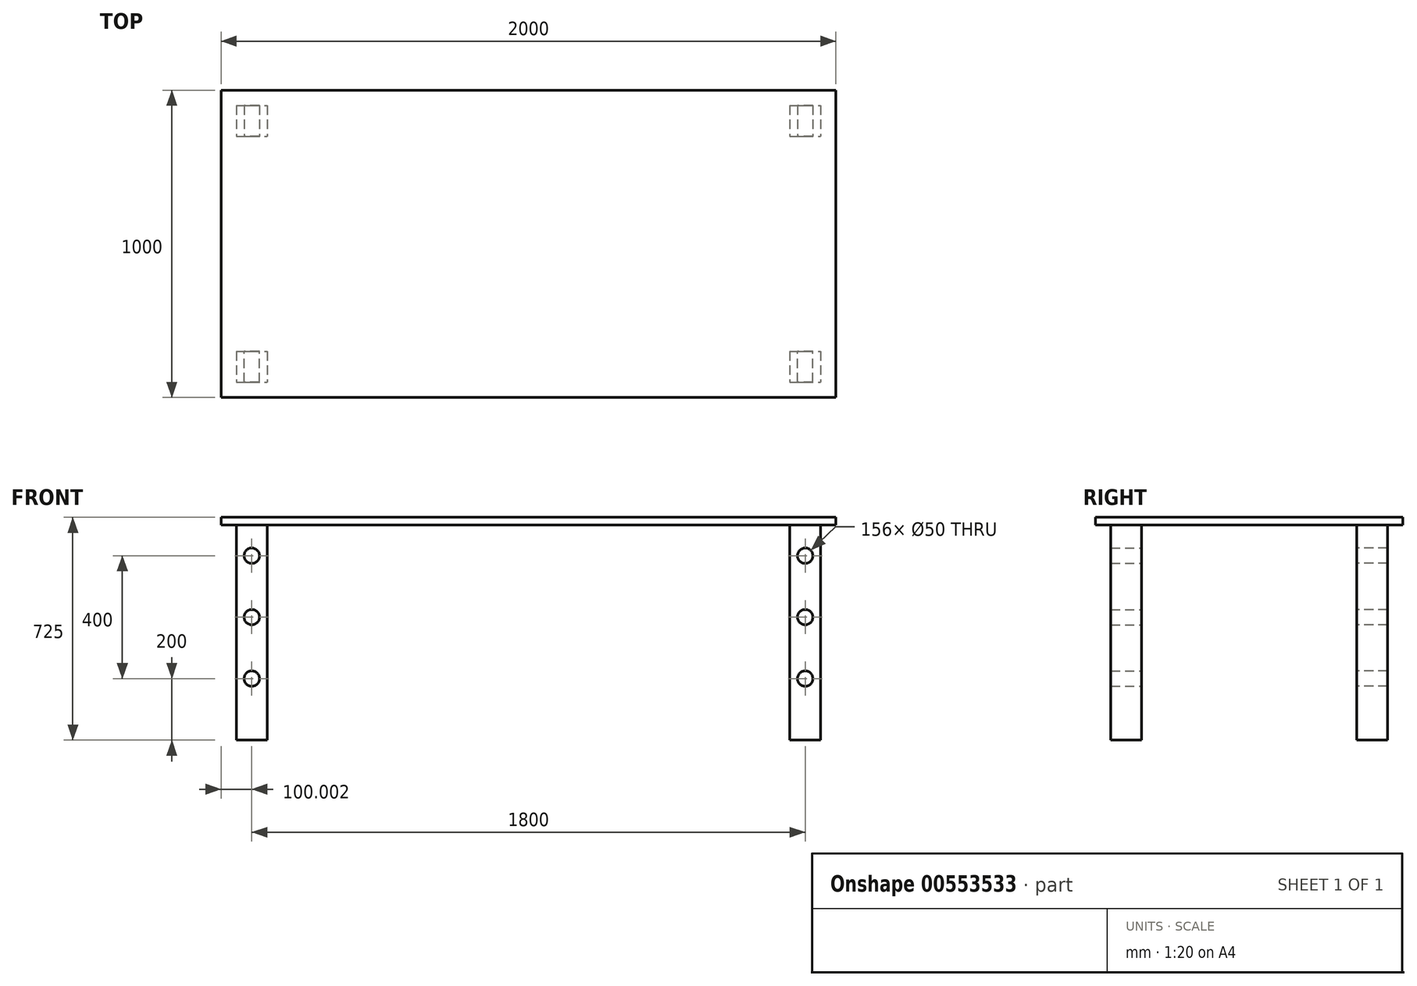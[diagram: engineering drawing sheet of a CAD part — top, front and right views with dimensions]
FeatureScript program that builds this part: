
annotation { "Feature Type Name" : "Feature", "Feature Type Description" : "" }
export const myFeature = defineFeature(function(context is Context, id is Id, definition is map)
    precondition{}
    {
        {
            var Q0;
            Q0=qCreatedBy(makeId("Top.planeOp"),FACE);
            var sketch = newSketch(context, id + "F0", { "sketchPlane" : qUnion([Q0])});
            skLineSegment(sketch, "E0.bottom", {"start": v(-1007.05, 533.18) * mm, "end": v(992.95, 533.18) * mm});
            skLineSegment(sketch, "E0.top", {"start": v(-1007.05, -466.82) * mm, "end": v(992.95, -466.82) * mm});
            skLineSegment(sketch, "E0.left", {"start": v(-1007.05, 533.18) * mm, "end": v(-1007.05, -466.82) * mm});
            skLineSegment(sketch, "E0.right", {"start": v(992.95, 533.18) * mm, "end": v(992.95, -466.82) * mm});
            skLineSegment(sketch, "E1.bottom", {"start": v(-957.05, 483.18) * mm, "end": v(-857.05, 483.18) * mm});
            skLineSegment(sketch, "E1.top", {"start": v(-957.05, 383.18) * mm, "end": v(-857.05, 383.18) * mm});
            skLineSegment(sketch, "E1.left", {"start": v(-957.05, 483.18) * mm, "end": v(-957.05, 383.18) * mm});
            skLineSegment(sketch, "E1.right", {"start": v(-857.05, 483.18) * mm, "end": v(-857.05, 383.18) * mm});
            skLineSegment(sketch, "E2.bottom", {"start": v(-957.05, -316.82) * mm, "end": v(-857.05, -316.82) * mm});
            skLineSegment(sketch, "E2.top", {"start": v(-957.05, -416.82) * mm, "end": v(-857.05, -416.82) * mm});
            skLineSegment(sketch, "E2.left", {"start": v(-957.05, -316.82) * mm, "end": v(-957.05, -416.82) * mm});
            skLineSegment(sketch, "E2.right", {"start": v(-857.05, -316.82) * mm, "end": v(-857.05, -416.82) * mm});
            skLineSegment(sketch, "E3.bottom", {"start": v(842.95, 483.18) * mm, "end": v(942.95, 483.18) * mm});
            skLineSegment(sketch, "E3.top", {"start": v(842.95, 383.18) * mm, "end": v(942.95, 383.18) * mm});
            skLineSegment(sketch, "E3.left", {"start": v(842.95, 483.18) * mm, "end": v(842.95, 383.18) * mm});
            skLineSegment(sketch, "E3.right", {"start": v(942.95, 483.18) * mm, "end": v(942.95, 383.18) * mm});
            skLineSegment(sketch, "E4.bottom", {"start": v(842.95, -316.82) * mm, "end": v(942.95, -316.82) * mm});
            skLineSegment(sketch, "E4.top", {"start": v(842.95, -416.82) * mm, "end": v(942.95, -416.82) * mm});
            skLineSegment(sketch, "E4.left", {"start": v(842.95, -316.82) * mm, "end": v(842.95, -416.82) * mm});
            skLineSegment(sketch, "E4.right", {"start": v(942.95, -316.82) * mm, "end": v(942.95, -416.82) * mm});
            skSolve(sketch);
        }
        {
            var Q0;
            Q0=makeQuery(id+"F0.imprint","IMPRINT",FACE,{"disambiguationData":[TD([[makeQuery(id+"F0.imprint","IMPRINT",EDGE,{"derivedFrom":sQuery(id+"F0.wireOp",EDGE,"E1.bottom")}),-1.0]])]});
            var Q1;
            Q1=makeQuery(id+"F0.imprint","IMPRINT",FACE,{"disambiguationData":[TD([[makeQuery(id+"F0.imprint","IMPRINT",EDGE,{"derivedFrom":sQuery(id+"F0.wireOp",EDGE,"E2.bottom")}),-1.0]])]});
            var Q2;
            Q2=makeQuery(id+"F0.imprint","IMPRINT",FACE,{"disambiguationData":[TD([[makeQuery(id+"F0.imprint","IMPRINT",EDGE,{"derivedFrom":sQuery(id+"F0.wireOp",EDGE,"E3.bottom")}),-1.0]])]});
            var Q3;
            Q3=makeQuery(id+"F0.imprint","IMPRINT",FACE,{"disambiguationData":[TD([[makeQuery(id+"F0.imprint","IMPRINT",EDGE,{"derivedFrom":sQuery(id+"F0.wireOp",EDGE,"E4.bottom")}),-1.0]])]});
            var Q4;
            Q4=makeQuery(id+"F0.imprint","IMPRINT",FACE,{"disambiguationData":[TD([[makeQuery(id+"F0.imprint","IMPRINT",EDGE,{"derivedFrom":sQuery(id+"F0.wireOp",EDGE,"E0.bottom")}),-1.0]])]});
            extrude(context, id + "F1", {"entities" : qUnion([Q0, Q1, Q2, Q3, Q4]), "depth" : 25 * mm, "offsetDistance" : 25 * mm});
        }
        {
            var Q0;
            Q0=makeQuery(id+"F0.imprint","IMPRINT",FACE,{"disambiguationData":[TD([[makeQuery(id+"F0.imprint","IMPRINT",EDGE,{"derivedFrom":sQuery(id+"F0.wireOp",EDGE,"E2.bottom")}),-1.0]])]});
            var Q1;
            Q1=makeQuery(id+"F0.imprint","IMPRINT",FACE,{"disambiguationData":[TD([[makeQuery(id+"F0.imprint","IMPRINT",EDGE,{"derivedFrom":sQuery(id+"F0.wireOp",EDGE,"E1.bottom")}),-1.0]])]});
            var Q2;
            Q2=makeQuery(id+"F0.imprint","IMPRINT",FACE,{"disambiguationData":[TD([[makeQuery(id+"F0.imprint","IMPRINT",EDGE,{"derivedFrom":sQuery(id+"F0.wireOp",EDGE,"E4.bottom")}),-1.0]])]});
            var Q3;
            Q3=makeQuery(id+"F0.imprint","IMPRINT",FACE,{"disambiguationData":[TD([[makeQuery(id+"F0.imprint","IMPRINT",EDGE,{"derivedFrom":sQuery(id+"F0.wireOp",EDGE,"E3.bottom")}),-1.0]])]});
            extrude(context, id + "F2", {"entities" : qUnion([Q0, Q1, Q2, Q3]), "oppositeDirection" : true, "depth" : 700 * mm, "offsetDistance" : 25 * mm});
        }
        {
            var Q0;
            Q0=qCreatedBy(makeId("Front.planeOp"),FACE);
            var sketch = newSketch(context, id + "F3", { "sketchPlane" : qUnion([Q0])});
            skCircle(sketch, "E5", {"center": v(-907.05, -500) * mm, "radius": 25 * mm});
            skCircle(sketch, "E6", {"center": v(-907.05, -300) * mm, "radius": 25 * mm});
            skCircle(sketch, "E7", {"center": v(-907.05, -100) * mm, "radius": 25 * mm});
            skCircle(sketch, "E8", {"center": v(892.95, -100) * mm, "radius": 25 * mm});
            skCircle(sketch, "E9", {"center": v(892.95, -300) * mm, "radius": 25 * mm});
            skCircle(sketch, "E10", {"center": v(892.95, -500) * mm, "radius": 25 * mm});
            skSolve(sketch);
        }
        {
            var Q0;
            Q0=sQuery(id+"F3.wireOp",VERTEX,"E7.center");
            var Q1;
            Q1=sQuery(id+"F3.wireOp",VERTEX,"E6.center");
            var Q2;
            Q2=sQuery(id+"F3.wireOp",VERTEX,"E5.center");
            var Q3;
            Q3=makeQuery(id+"F2.opExtrude","SWEPT_BODY",BODY,{"disambiguationData":[OSD([sQuery(id+"F0.wireOp",EDGE,"E2.bottom"),sQuery(id+"F0.wireOp",EDGE,"E2.top"),sQuery(id+"F0.wireOp",EDGE,"E2.left"),sQuery(id+"F0.wireOp",EDGE,"E2.right")])]});
            hole(context, id + "F4", {"style" : HoleStyle.SIMPLE, "endStyle" : HoleEndStyle.THROUGH, "oppositeDirection" : true, "holeDiameter" : 50 * mm, "isTappedThrough" : true, "tappedDepth" : 12 * mm, "tapClearance" : 3, "locations" : qUnion([Q0, Q1, Q2]), "scope" : qUnion([Q3])});
        }
        {
            var Q0;
            Q0=sQuery(id+"F3.wireOp",VERTEX,"E7.center");
            var Q1;
            Q1=sQuery(id+"F3.wireOp",VERTEX,"E6.center");
            var Q2;
            Q2=sQuery(id+"F3.wireOp",VERTEX,"E5.center");
            var Q3;
            Q3=makeQuery(id+"F2.opExtrude","SWEPT_BODY",BODY,{"disambiguationData":[OSD([sQuery(id+"F0.wireOp",EDGE,"E1.bottom"),sQuery(id+"F0.wireOp",EDGE,"E1.top"),sQuery(id+"F0.wireOp",EDGE,"E1.left"),sQuery(id+"F0.wireOp",EDGE,"E1.right")])]});
            hole(context, id + "F5", {"style" : HoleStyle.SIMPLE, "endStyle" : HoleEndStyle.THROUGH, "holeDiameter" : 50 * mm, "isTappedThrough" : true, "tappedDepth" : 12 * mm, "tapClearance" : 3, "locations" : qUnion([Q0, Q1, Q2]), "scope" : qUnion([Q3])});
        }
        {
            var Q0;
            Q0=sQuery(id+"F3.wireOp",VERTEX,"E8.center");
            var Q1;
            Q1=sQuery(id+"F3.wireOp",VERTEX,"E9.center");
            var Q2;
            Q2=sQuery(id+"F3.wireOp",VERTEX,"E10.center");
            var Q3;
            Q3=makeQuery(id+"F2.opExtrude","SWEPT_BODY",BODY,{"disambiguationData":[OSD([sQuery(id+"F0.wireOp",EDGE,"E4.bottom"),sQuery(id+"F0.wireOp",EDGE,"E4.top"),sQuery(id+"F0.wireOp",EDGE,"E4.left"),sQuery(id+"F0.wireOp",EDGE,"E4.right")])]});
            hole(context, id + "F6", {"style" : HoleStyle.SIMPLE, "endStyle" : HoleEndStyle.THROUGH, "oppositeDirection" : true, "holeDiameter" : 50 * mm, "isTappedThrough" : true, "tappedDepth" : 12 * mm, "tapClearance" : 3, "locations" : qUnion([Q0, Q1, Q2]), "scope" : qUnion([Q3])});
        }
        {
            var Q0;
            Q0=sQuery(id+"F3.wireOp",VERTEX,"E8.center");
            var Q1;
            Q1=sQuery(id+"F3.wireOp",VERTEX,"E9.center");
            var Q2;
            Q2=sQuery(id+"F3.wireOp",VERTEX,"E10.center");
            var Q3;
            Q3=makeQuery(id+"F2.opExtrude","SWEPT_BODY",BODY,{"disambiguationData":[OSD([sQuery(id+"F0.wireOp",EDGE,"E3.bottom"),sQuery(id+"F0.wireOp",EDGE,"E3.top"),sQuery(id+"F0.wireOp",EDGE,"E3.left"),sQuery(id+"F0.wireOp",EDGE,"E3.right")])]});
            hole(context, id + "F7", {"style" : HoleStyle.SIMPLE, "endStyle" : HoleEndStyle.THROUGH, "holeDiameter" : 50 * mm, "isTappedThrough" : true, "tappedDepth" : 12 * mm, "tapClearance" : 3, "locations" : qUnion([Q0, Q1, Q2]), "scope" : qUnion([Q3])});
        }
    });
